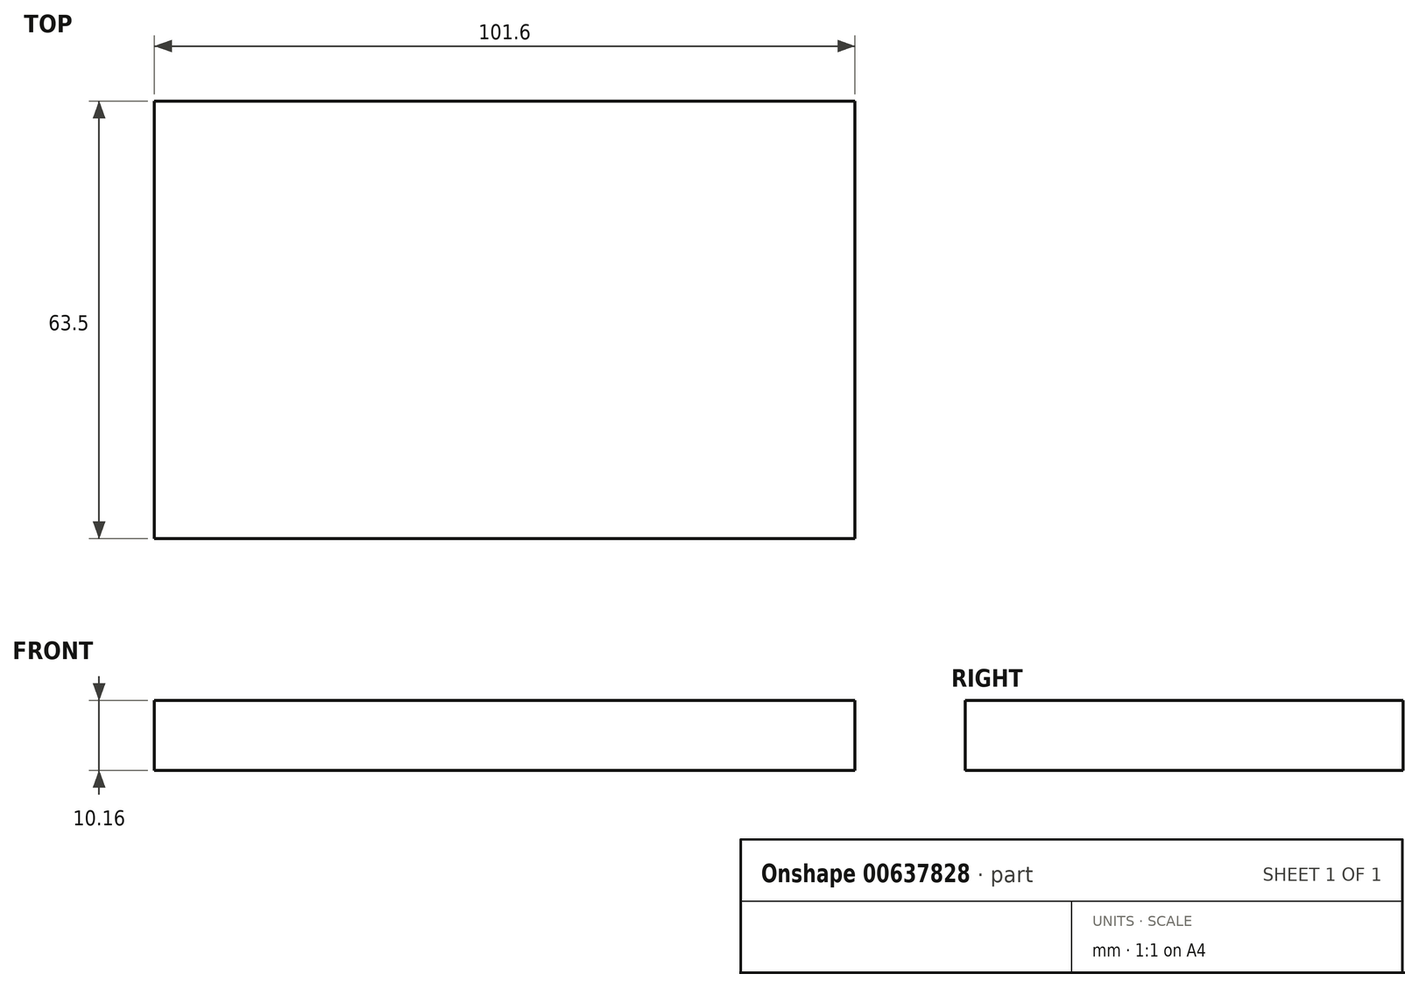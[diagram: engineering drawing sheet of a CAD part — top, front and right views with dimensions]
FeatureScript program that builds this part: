
annotation { "Feature Type Name" : "Feature", "Feature Type Description" : "" }
export const myFeature = defineFeature(function(context is Context, id is Id, definition is map)
    precondition{}
    {
        {
            var Q0;
            Q0=qCreatedBy(makeId("Top.planeOp"),FACE);
            var sketch = newSketch(context, id + "F0", { "sketchPlane" : qUnion([Q0])});
            skLineSegment(sketch, "E0.bottom", {"start": v(50.8, -31.75) * mm, "end": v(-50.8, -31.75) * mm});
            skLineSegment(sketch, "E0.top", {"start": v(50.8, 31.75) * mm, "end": v(-50.8, 31.75) * mm});
            skLineSegment(sketch, "E0.left", {"start": v(50.8, -31.75) * mm, "end": v(50.8, 31.75) * mm});
            skLineSegment(sketch, "E0.right", {"start": v(-50.8, -31.75) * mm, "end": v(-50.8, 31.75) * mm});
            skPoint(sketch, "E0.middle", {"position": v(0, 0) * mm});
            skSolve(sketch);
        }
        {
            var Q0;
            Q0 = qSketchRegion(id + "F0", true);
            extrude(context, id + "F1", {"entities" : qUnion([Q0]), "depth" : 10.16 * mm, "offsetDistance" : 25.4 * mm});
        }
    });
